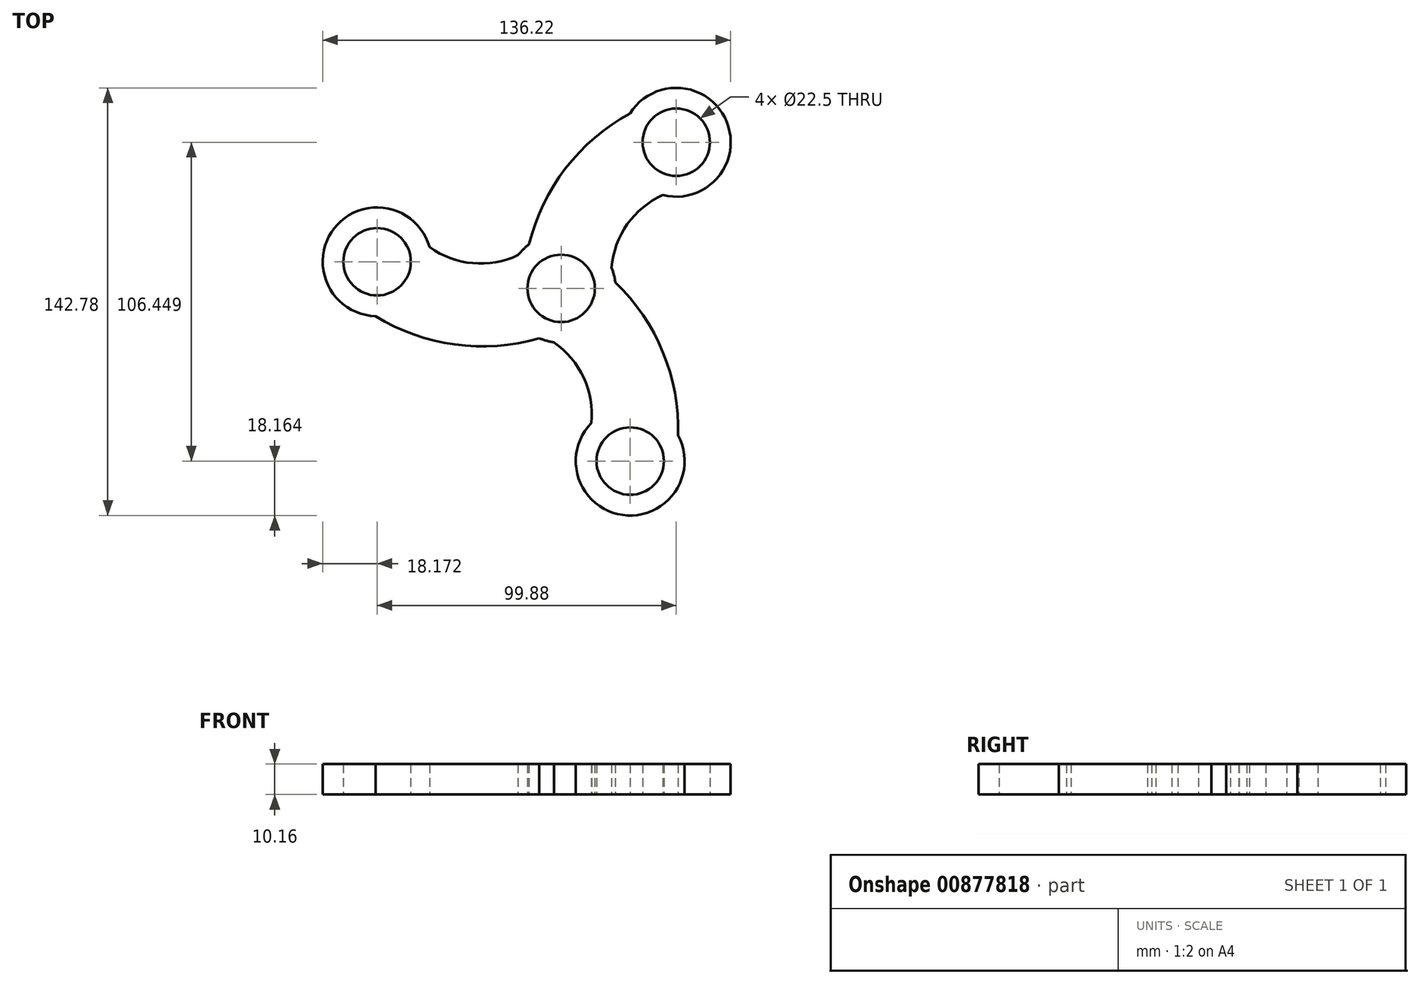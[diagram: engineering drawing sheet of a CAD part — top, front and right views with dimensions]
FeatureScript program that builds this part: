
annotation { "Feature Type Name" : "Feature", "Feature Type Description" : "" }
export const myFeature = defineFeature(function(context is Context, id is Id, definition is map)
    precondition{}
    {
        {
            var Q0;
            Q0=qCreatedBy(makeId("Top.planeOp"),FACE);
            var sketch = newSketch(context, id + "F0", { "sketchPlane" : qUnion([Q0])});
            skCircle(sketch, "E0", {"center": v(0, 0) * mm, "radius": 11.25 * mm});
            skCircle(sketch, "E1", {"center": v(38.42, 48.78) * mm, "radius": 11.25 * mm});
            skCircle(sketch, "E2", {"center": v(0, 0) * mm, "radius": 18.17 * mm});
            skCircle(sketch, "E3", {"center": v(38.42, 48.78) * mm, "radius": 18.17 * mm});
            skArc(sketch, "E4", {"start": v(22.97, 58.34) * mm, "mid": v(1.48, 40.09) * mm, "end": v(-10.72, 14.67) * mm});
            skArc(sketch, "E5", {"start": v(33.9, 31.19) * mm, "mid": v(22.06, 21.38) * mm, "end": v(16.8, 6.93) * mm});
            skCircle(sketch, "E6.1.0", {"center": v(-61.46, 8.88) * mm, "radius": 18.17 * mm});
            skCircle(sketch, "E6.1.1", {"center": v(-61.46, 8.88) * mm, "radius": 11.25 * mm});
            skArc(sketch, "E6.1.2", {"start": v(-43.96, 13.76) * mm, "mid": v(-29.54, 8.42) * mm, "end": v(-14.4, 11.08) * mm});
            skArc(sketch, "E6.1.3", {"start": v(-62, -9.28) * mm, "mid": v(-35.46, -18.76) * mm, "end": v(-7.34, -16.62) * mm});
            skCircle(sketch, "E6.2.0", {"center": v(23.04, -57.67) * mm, "radius": 18.17 * mm});
            skCircle(sketch, "E6.2.1", {"center": v(23.04, -57.67) * mm, "radius": 11.25 * mm});
            skArc(sketch, "E6.2.2", {"start": v(10.06, -44.95) * mm, "mid": v(7.48, -29.8) * mm, "end": v(-2.4, -18) * mm});
            skArc(sketch, "E6.2.3", {"start": v(39.04, -49.06) * mm, "mid": v(33.97, -21.33) * mm, "end": v(18.06, 1.95) * mm});
            skSolve(sketch);
        }
        {
            var Q0;
            {var subQ0=sQuery(id+"F0.wireOp",EDGE,"E4");Q0=makeQuery(id+"F0.imprint","IMPRINT",FACE,{"disambiguationData":[TD([[makeQuery(id+"F0.imprint","IMPRINT",EDGE,{"derivedFrom":subQ0}),1.0]])]});}
            var Q1;
            Q1=makeQuery(id+"F0.imprint","IMPRINT",FACE,{"disambiguationData":[TD([[makeQuery(id+"F0.imprint","IMPRINT",EDGE,{"derivedFrom":sQuery(id+"F0.wireOp",EDGE,"E1")}),-1.0]])]});
            var Q2;
            {var subQ0=sQuery(id+"F0.wireOp",EDGE,"E6.2.2");Q2=makeQuery(id+"F0.imprint","IMPRINT",FACE,{"disambiguationData":[TD([[makeQuery(id+"F0.imprint","IMPRINT",EDGE,{"derivedFrom":subQ0}),-1.0]])]});}
            var Q3;
            Q3=makeQuery(id+"F0.imprint","IMPRINT",FACE,{"disambiguationData":[TD([[makeQuery(id+"F0.imprint","IMPRINT",EDGE,{"derivedFrom":sQuery(id+"F0.wireOp",EDGE,"E0")}),-1.0]])]});
            var Q4;
            Q4=makeQuery(id+"F0.imprint","IMPRINT",FACE,{"disambiguationData":[TD([[makeQuery(id+"F0.imprint","IMPRINT",EDGE,{"derivedFrom":sQuery(id+"F0.wireOp",EDGE,"E6.1.1")}),-1.0]])]});
            var Q5;
            {var subQ0=sQuery(id+"F0.wireOp",EDGE,"E6.1.2");Q5=makeQuery(id+"F0.imprint","IMPRINT",FACE,{"disambiguationData":[TD([[makeQuery(id+"F0.imprint","IMPRINT",EDGE,{"derivedFrom":subQ0}),-1.0]])]});}
            var Q6;
            Q6=makeQuery(id+"F0.imprint","IMPRINT",FACE,{"disambiguationData":[TD([[makeQuery(id+"F0.imprint","IMPRINT",EDGE,{"derivedFrom":sQuery(id+"F0.wireOp",EDGE,"E6.2.1")}),-1.0]])]});
            extrude(context, id + "F1", {"entities" : qUnion([Q0, Q1, Q2, Q3, Q4, Q5, Q6]), "depth" : 10.16 * mm, "offsetDistance" : 25.4 * mm});
        }
    });
